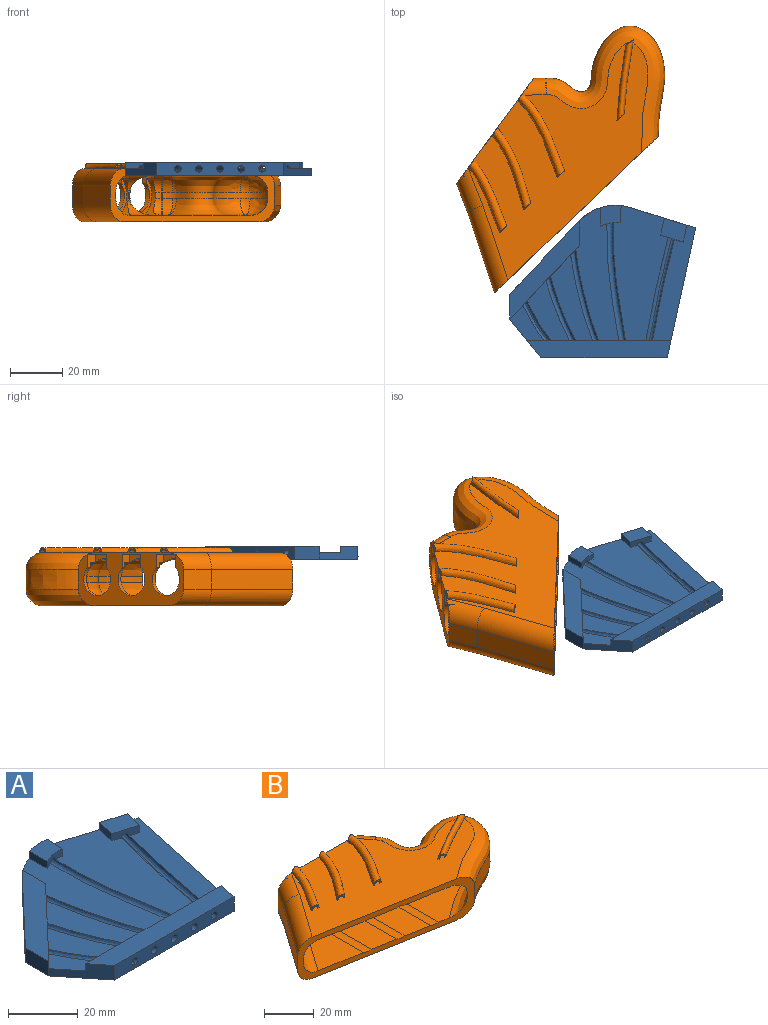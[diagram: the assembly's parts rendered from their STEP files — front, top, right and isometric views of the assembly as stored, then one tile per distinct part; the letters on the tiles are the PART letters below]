
ASSEMBLY  parts=2 mates=1
PART A: 43 faces, bbox 73.4x60.9x7.5 mm
  f0: bspline ~35.85x9.52mm, area 0mm2, adj f13,f41
  f1: bspline ~2.54x1.27mm, area 0mm2, adj f13,f38
  f2: plane 28.04x26.67mm, normal (-0.72,0.69,0), area 180.7mm2, adj f7,f11,f15,f16,f18,f31,f33,f35
  f3: plane 23.54x16.85mm, normal (0,0,1), area 166.3mm2, adj f17,f19,f33,f39
  f4: plane 33.35x16.58mm, normal (0,0,1), area 230.2mm2, adj f17,f19,f31,f33
  f5: plane 50.96x16.52mm, normal (0,0,1), area 493.6mm2, adj f7,f16,f17,f19,f25,f26,f30,f31
  f6: plane 52.57x21.9mm, normal (0,0,1), area 752.6mm2, adj f7,f9,f19,f21,f22,f26,f27,f30
  f7: cylinder r=19.05mm len=19.49mm, axis (0,0,-1), area 68.8mm2, adj f2,f5,f6,f9,f15,f25,f27,f28
  f8: plane 44.14x16.45mm, normal (0,0,1), area 301.2mm2, adj f9,f14,f19,f22,f23,f29
  f9: plane 25.47x8.38mm, normal (0.3,0.95,0), area 84.2mm2, adj f6,f7,f8,f14,f15,f21,f23,f24
  f10: plane 14.06x13.65mm, normal (0,0,1), area 78.8mm2, adj f12,f17,f19,f35
  f11: plane 9.53x5.08mm, normal (-1,0,0), area 48.4mm2, adj f2,f12,f15,f17,f18
  f12: plane 14.85x11.94mm, normal (-0.78,-0.63,0), area 69.8mm2, adj f10,f11,f13,f15,f19,f20
  f13: plane 48.62x5.44mm, normal (0,-1,0), area 219.8mm2, adj f0,f1,f12,f14,f15,f20,f29,f30
  f14: plane 49.64x10.8mm, normal (0.98,-0.21,0), area 146.1mm2, adj f8,f9,f13,f15,f19,f20
  f15: plane 70.99x58.29mm, normal (0,0,-1), area 3105.9mm2, adj f2,f7,f9,f11,f12,f13,f14
  f16: plane 9.53x2.54mm, normal (1,0,0), area 24.2mm2, adj f2,f5,f17,f18
  f17: plane 28.85x27.48mm, normal (0.72,-0.69,0), area 90.5mm2, adj f3,f4,f5,f10,f11,f16,f18,f31
  f18: plane 37.52x26.63mm, normal (0,0,1), area 253.6mm2, adj f2,f11,f16,f17
  f19: plane 55.52x3.09mm, normal (0,1,0), area 127.1mm2, adj f3,f4,f5,f6,f8,f10,f12,f14
  f20: plane 54.97x6.56mm, normal (0,0,1), area 338.8mm2, adj f12,f13,f14,f19
  f21: plane 6.44x2.54mm, normal (-0.98,0.21,0), area 16.7mm2, adj f6,f9,f22,f24
  f22: plane 9.03x3.09mm, normal (-0.3,-0.95,0), area 20.5mm2, adj f6,f8,f21,f23,f24,f29,f42
  f23: plane 6.44x2.54mm, normal (0.98,-0.21,0), area 16.7mm2, adj f8,f9,f22,f24
  f24: plane 10.04x9.14mm, normal (0,0,1), area 59.4mm2, adj f9,f21,f22,f23
  f25: plane 7.06x2.54mm, normal (-1,0,0), area 17.9mm2, adj f5,f7,f26,f28
  f26: cylinder r=12.49mm len=7.38mm, axis (0,0,-1), area 16.7mm2, adj f5,f6,f25,f27,f28,f30
  f27: plane 6.56x2.54mm, normal (1,-0.07,0), area 16.7mm2, adj f6,f7,f26,f28
  f28: plane 7.91x7.82mm, normal (0,0,1), area 50.8mm2, adj f7,f25,f26,f27
  f29: bspline ~52.02x12.49mm, area 131.9mm2, adj f8,f9,f13,f19,f22,f42
  f30: bspline ~58.48x8.55mm, area 285.4mm2, adj f5,f6,f7,f13,f19,f26,f40
  f31: bspline ~50.06x14.6mm, area 247.9mm2, adj f2,f4,f5,f13,f17,f19,f32
  f32: plane 2.9x1.45mm, normal (-0.52,-0.86,0), area 0.5mm2, adj f31,f36
  f33: bspline ~38.99x17.09mm, area 205.2mm2, adj f2,f3,f4,f13,f17,f19,f34
  f34: plane 2.9x1.47mm, normal (-0.49,-0.87,0), area 0.2mm2, adj f33,f37
  f35: bspline ~27.69x19.66mm, area 83.1mm2, adj f2,f10,f13,f17,f19,f39
  f36: bspline ~35.53x6.59mm, area 3.3mm2, adj f2,f32
  f37: bspline ~26.5x8.08mm, area 3.5mm2, adj f2,f34
  f38: plane 4.99x3.58mm, normal (-0.89,0.45,0), area 0.5mm2, adj f1,f39
  f39: bspline ~28.25x17.74mm, area 90.7mm2, adj f2,f3,f17,f19,f35,f38
  f40: cylinder r=1.27mm len=1.27mm, axis (-0.22,-0.98,0), area 0mm2, adj f7,f30
  f41: plane 3.14x1.84mm, normal (0.22,0.98,0), area 0mm2, adj f0,f42
  f42: bspline ~52.78x13.7mm, area 132.4mm2, adj f6,f9,f19,f22,f29,f41
PART B: 109 faces, bbox 116.8x88.5x26.4 mm
  f0: plane 101.29x50.09mm, normal (0,0,1), area 2881.5mm2, adj f1,f2,f4,f5,f6,f7,f8,f9
  f1: plane 2.45x2.35mm, normal (-0.31,0.95,0), area 1.6mm2, adj f0,f2,f4,f103
  f2: bspline ~30.89x18.18mm, area 192mm2, adj f0,f1,f3,f100,f103
  f3: plane 0.94x0.62mm, normal (0,0,-1), area 0.4mm2, adj f2,f4,f74,f103
  f4: bspline ~30.59x16.95mm, area 128mm2, adj f0,f1,f3,f100,f103
  f5: plane 2.45x2.39mm, normal (-0.23,0.97,0), area 1.6mm2, adj f0,f6,f7,f11
  f6: bspline ~27.63x19.45mm, area 176.7mm2, adj f0,f5,f11,f101
  f7: bspline ~27.38x18.21mm, area 117.9mm2, adj f0,f5,f11,f101
  f8: plane 2.45x2.41mm, normal (-0.19,0.98,0), area 1.6mm2, adj f0,f9,f10,f11
  f9: bspline ~25.33x16.73mm, area 160.7mm2, adj f0,f8,f11,f102
  f10: bspline ~25.1x15.49mm, area 107.3mm2, adj f0,f8,f11,f102
  f11: plane 51.9x24.23mm, normal (0,1,0), area 492.5mm2, adj f0,f5,f6,f7,f8,f9,f10,f12
  f12: cylinder r=6.35mm len=16.48mm, axis (0.53,0.85,0), area 128mm2, adj f0,f11,f36,f80,f97,f99
  f13: cylinder r=6.35mm len=12.7mm, axis (0,1,0), area 53.4mm2, adj f11,f83,f97,f98
  f14: cylinder r=7.87mm len=40.82mm, axis (0,1,0), area 421.7mm2, adj f16,f17,f20,f23,f26,f27,f29,f30
  f15: cylinder r=6.35mm len=12.31mm, axis (-1,0,0), area 60.1mm2, adj f22,f28,f84,f87
  f16: cylinder r=6.35mm len=12.31mm, axis (-1,0,0), area 60.1mm2, adj f14,f23,f27,f84
  f17: cylinder r=6.35mm len=2.67mm, axis (-1,0,0), area 2.2mm2, adj f14,f29,f44
  f18: cylinder r=6.35mm len=3.61mm, axis (1,0,0), area 4.7mm2, adj f24,f70,f87
  f19: cylinder r=6.35mm len=12.31mm, axis (1,0,0), area 60.1mm2, adj f25,f28,f84,f87
  f20: cylinder r=6.35mm len=12.31mm, axis (1,0,0), area 60.1mm2, adj f14,f26,f27,f84
  f21: plane 40.39x37.68mm, normal (0,0,-1), area 626.4mm2, adj f31,f34,f49,f55,f61,f62,f65,f87
  f22: plane 38.79x12.31mm, normal (0,0,-1), area 463.9mm2, adj f15,f34,f84,f87
  f23: plane 35.89x12.31mm, normal (0,0,-1), area 428.3mm2, adj f14,f16,f34,f84
  f24: plane 40.39x37.68mm, normal (0,0,1), area 626.4mm2, adj f18,f34,f56,f63,f69,f71,f72,f87
  f25: plane 38.79x12.31mm, normal (0,0,1), area 463.9mm2, adj f19,f34,f84,f87
  f26: plane 35.89x12.31mm, normal (0,0,1), area 428.3mm2, adj f14,f20,f34,f84
  f27: plane 2.54x0.73mm, normal (0,-1,0), area 1.5mm2, adj f14,f16,f20,f84
  f28: plane 2.54x0.73mm, normal (0,-1,0), area 1.5mm2, adj f15,f19,f84,f87
  f29: sphere r=6.35mm, area 21.1mm2, adj f14,f17,f30,f54
  f30: cylinder r=6.35mm len=2.54mm, axis (0,0,1), area 4.3mm2, adj f14,f29,f32,f41
  f31: cylinder r=6.35mm len=3.61mm, axis (-1,0,0), area 4.7mm2, adj f21,f64,f87
  f32: sphere r=6.35mm, area 21.1mm2, adj f14,f30,f33,f60
  f33: cylinder r=6.35mm len=2.67mm, axis (1,0,0), area 2.2mm2, adj f14,f32,f45
  f34: plane 87.5x22.6mm, normal (-0.18,-0.98,0), area 532.5mm2, adj f0,f14,f21,f22,f23,f24,f25,f26
  f35: plane 7.62x3.72mm, normal (0.8,0.6,0), area 35.5mm2, adj f11,f74,f75,f79
  f36: plane 9.56x7.62mm, normal (-0.85,0.53,0), area 86.1mm2, adj f11,f12,f37,f47
  f37: plane 26.73x18.96mm, normal (-0.82,0.58,0), area 249.7mm2, adj f34,f36,f46,f80
  f38: extruded ~47.69x36.76mm, area 745.5mm2, adj f34,f73,f76,f79
  f39: plane 101.29x49.9mm, normal (0,0,-1), area 3021.8mm2, adj f11,f34,f46,f47,f75,f76,f78
  f40: plane 2.54x0.18mm, normal (-0.8,-0.6,0), area 0.6mm2, adj f61,f67,f68,f72
  f41: plane 5.33x3.36mm, normal (0.85,-0.53,0), area 16mm2, adj f30,f53,f54,f60
  f42: plane 25.67x18.21mm, normal (0.82,-0.58,0), area 79.9mm2, adj f34,f48,f52,f53
  f43: extruded ~45.53x36.32mm, area 246.3mm2, adj f34,f49,f51,f55,f56,f58,f59,f62
  f44: plane 33x21.78mm, normal (0,0,-1), area 377mm2, adj f14,f17,f34,f48,f50,f54
  f45: plane 33x21.78mm, normal (0,0,1), area 377mm2, adj f14,f33,f34,f52,f57,f60
  f46: cylinder r=6.35mm len=30.55mm, axis (-0.58,-0.82,0), area 312.8mm2, adj f34,f37,f39,f47
  f47: cylinder r=6.35mm len=16.48mm, axis (-0.53,-0.85,0), area 133.6mm2, adj f11,f36,f39,f46
  f48: cylinder r=6.35mm len=29.34mm, axis (-0.58,-0.82,0), area 299mm2, adj f34,f42,f44,f50
  f49: bspline ~78.02x62.2mm, area 455.8mm2, adj f21,f34,f43,f51
  f50: torus R=12.7mm, axis (0,0,1), area 4.7mm2, adj f44,f48,f53,f54
  f51: bspline ~6.35x5.92mm, area 15.2mm2, adj f43,f49,f55
  f52: cylinder r=6.35mm len=29.34mm, axis (0.58,0.82,0), area 299mm2, adj f34,f42,f45,f57
  f53: cylinder r=6.35mm len=2.54mm, axis (0,0,-1), area 0.9mm2, adj f41,f42,f50,f57
  f54: cylinder r=6.35mm len=8.73mm, axis (-0.53,-0.85,0), area 62.8mm2, adj f29,f41,f44,f50
  f55: bspline ~37.58x18.05mm, area 432.1mm2, adj f21,f43,f51,f58
  f56: bspline ~78.02x62.2mm, area 455.7mm2, adj f24,f34,f43,f59
  f57: torus R=12.7mm, axis (0,0,1), area 4.7mm2, adj f45,f52,f53,f60
  f58: bspline ~6.35x6.31mm, area 5.4mm2, adj f43,f55,f62
  f59: bspline ~6.35x5.92mm, area 12.6mm2, adj f43,f56,f63
  f60: cylinder r=6.35mm len=8.73mm, axis (0.53,0.85,0), area 62.8mm2, adj f32,f41,f45,f57
  f61: cylinder r=6.35mm len=6.35mm, axis (-0.6,0.8,0), area 2.3mm2, adj f21,f40,f64,f65
  f62: bspline ~7.54x6.35mm, area 34mm2, adj f21,f43,f58,f65
  f63: bspline ~37.58x18.07mm, area 432.1mm2, adj f24,f43,f59,f66
  f64: sphere r=6.35mm, area 27.4mm2, adj f31,f61,f67,f87
  f65: torus R=12.7mm, axis (0,0,1), area 0.7mm2, adj f21,f61,f62,f68
  f66: bspline ~6.35x6.31mm, area 5.3mm2, adj f43,f63,f69
  f67: cylinder r=6.35mm len=2.54mm, axis (0,0,-1), area 6.1mm2, adj f40,f64,f70,f87
  f68: cylinder r=6.35mm len=2.54mm, axis (0,0,-1), area 0.1mm2, adj f40,f43,f65,f71
  f69: bspline ~7.54x6.35mm, area 34mm2, adj f24,f43,f66,f71
  f70: sphere r=6.35mm, area 27.4mm2, adj f18,f67,f72,f87
  f71: torus R=12.7mm, axis (0,0,1), area 0.7mm2, adj f24,f68,f69,f72
  f72: cylinder r=6.35mm len=6.35mm, axis (0.6,-0.8,0), area 2.3mm2, adj f24,f40,f70,f71
  f73: bspline ~56.25x43.94mm, area 958.1mm2, adj f0,f34,f38,f77,f107
  f74: cylinder r=6.35mm len=11.36mm, axis (0.6,-0.8,0), area 63.7mm2, adj f0,f3,f11,f35,f77,f88,f91
  f75: cylinder r=6.35mm len=11.36mm, axis (-0.6,0.8,0), area 70.3mm2, adj f11,f35,f39,f78
  f76: bspline ~56.25x43.94mm, area 966.6mm2, adj f34,f38,f39,f78
  f77: torus R=12.7mm, axis (0,0,1), area 0.7mm2, adj f0,f73,f74,f79
  f78: torus R=12.7mm, axis (0,0,1), area 0.7mm2, adj f39,f75,f76,f79
  f79: cylinder r=6.35mm len=7.62mm, axis (0,0,-1), area 0.4mm2, adj f35,f38,f77,f78
  f80: cylinder r=6.35mm len=30.55mm, axis (0.58,0.82,0), area 312.8mm2, adj f0,f12,f34,f37
  f81: cylinder r=6.35mm len=12.7mm, axis (0,1,0), area 53.4mm2, adj f11,f86,f88,f89
  f82: cylinder r=6.35mm len=12.7mm, axis (0,1,0), area 53.4mm2, adj f11,f85,f93,f94
  f83: plane 15.75x14.37mm, normal (0,-1,0), area 53.4mm2, adj f13,f14,f97,f98
  f84: cylinder r=7.87mm len=43.71mm, axis (0,1,0), area 419.2mm2, adj f15,f16,f19,f20,f22,f23,f25,f26
  f85: plane 15.75x14.37mm, normal (0,-1,0), area 53.4mm2, adj f82,f84,f93,f94
  f86: plane 15.75x14.37mm, normal (0,-1,0), area 53.4mm2, adj f81,f87,f88,f89
  f87: cylinder r=7.87mm len=46.61mm, axis (0,1,0), area 458.7mm2, adj f15,f18,f19,f21,f22,f24,f25,f28
  f88: plane 5.08x4.83mm, normal (-1,0,0), area 18.5mm2, adj f11,f74,f81,f86,f87,f90,f91
  f89: plane 5.08x4.83mm, normal (1,0,0), area 18.5mm2, adj f11,f81,f86,f87,f90,f91
  f90: plane 8.89x3.12mm, normal (0,1,0), area 19.4mm2, adj f87,f88,f89,f91
  f91: plane 8.89x4.83mm, normal (0,0,-1), area 42.9mm2, adj f11,f74,f88,f89,f90
  f92: plane 8.89x3.12mm, normal (0,1,0), area 19.4mm2, adj f84,f93,f94,f95
  f93: plane 5.08x4.83mm, normal (-1,0,0), area 18.5mm2, adj f11,f82,f84,f85,f92,f95
  f94: plane 5.08x4.83mm, normal (1,0,0), area 18.5mm2, adj f11,f82,f84,f85,f92,f95
  f95: plane 8.89x4.83mm, normal (0,0,-1), area 42.9mm2, adj f11,f92,f93,f94
  f96: plane 8.89x3.12mm, normal (0,1,0), area 19.4mm2, adj f14,f97,f98,f99
  f97: plane 5.09x4.83mm, normal (1,0,0), area 18.5mm2, adj f11,f12,f13,f14,f83,f96,f99
  f98: plane 5.08x4.83mm, normal (-1,0,0), area 18.5mm2, adj f11,f13,f14,f83,f96,f99
  f99: plane 8.89x4.83mm, normal (0,0,-1), area 42.7mm2, adj f11,f12,f96,f97,f98
  f100: plane 4.29x2.45mm, normal (-0.18,-0.98,0), area 3.2mm2, adj f0,f2,f4
  f101: plane 4.29x2.45mm, normal (-0.18,-0.98,0), area 3.2mm2, adj f0,f6,f7
  f102: plane 4.29x2.45mm, normal (-0.18,-0.98,0), area 3.2mm2, adj f0,f9,f10
  f103: plane 2.49x2.35mm, normal (0,1,0), area 1.5mm2, adj f1,f2,f3,f4
  f104: plane 4.29x2.45mm, normal (-0.18,-0.98,0), area 3.2mm2, adj f0,f106,f108
  f105: plane 4.2x2.45mm, normal (0.28,0.96,0), area 3.2mm2, adj f0,f106,f107,f108
  f106: bspline ~28.67x14.9mm, area 145.5mm2, adj f0,f104,f105,f107
  f107: plane 1.44x0.84mm, normal (0,0,-1), area 0.5mm2, adj f73,f105,f106,f108
  f108: bspline ~27.43x14.61mm, area 97mm2, adj f0,f104,f105,f107
PLACE A t=(-24.11,-28.72,3.31)mm
PLACE B rot(axis=(0,0,1),53.8deg) t=(-47.65,27.11,-14.47)mm
MATE planar B.f23 <-> A.f15  axis (0,0,-1) through (-21.24,40.29,3.31)mm
